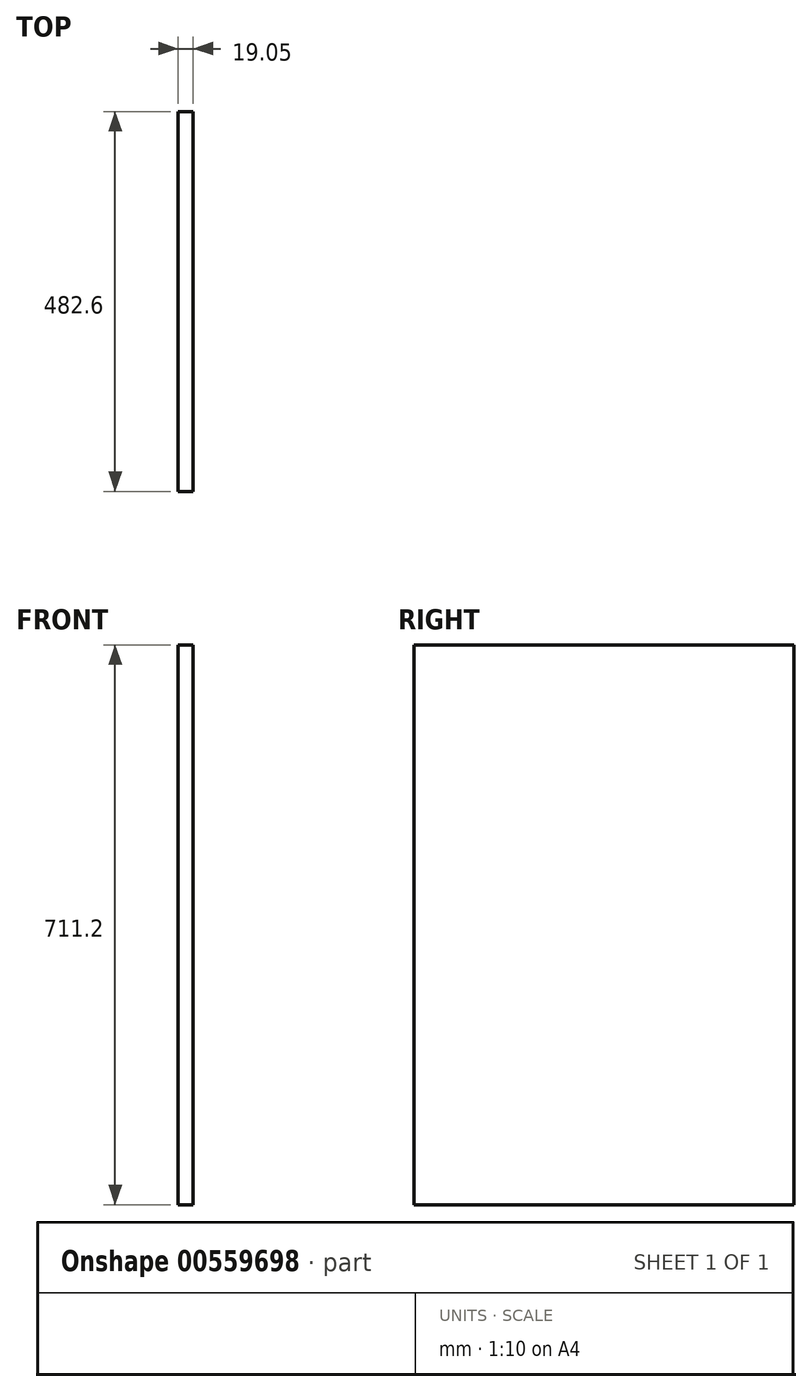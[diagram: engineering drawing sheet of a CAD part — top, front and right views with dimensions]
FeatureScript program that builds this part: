
annotation { "Feature Type Name" : "Feature", "Feature Type Description" : "" }
export const myFeature = defineFeature(function(context is Context, id is Id, definition is map)
    precondition{}
    {
        {
            var Q0;
            Q0=qCreatedBy(makeId("Right.planeOp"),FACE);
            var sketch = newSketch(context, id + "F0", { "sketchPlane" : qUnion([Q0])});
            skLineSegment(sketch, "E0.bottom", {"start": v(241.3, -355.6) * mm, "end": v(-241.3, -355.6) * mm});
            skLineSegment(sketch, "E0.top", {"start": v(241.3, 355.6) * mm, "end": v(-241.3, 355.6) * mm});
            skLineSegment(sketch, "E0.left", {"start": v(241.3, -355.6) * mm, "end": v(241.3, 355.6) * mm});
            skLineSegment(sketch, "E0.right", {"start": v(-241.3, -355.6) * mm, "end": v(-241.3, 355.6) * mm});
            skPoint(sketch, "E0.middle", {"position": v(0, 0) * mm});
            skSolve(sketch);
        }
        {
            var Q0;
            Q0 = qSketchRegion(id + "F0", true);
            extrude(context, id + "F1", {"entities" : qUnion([Q0]), "depth" : 19.05 * mm, "offsetDistance" : 25.4 * mm});
        }
    });
